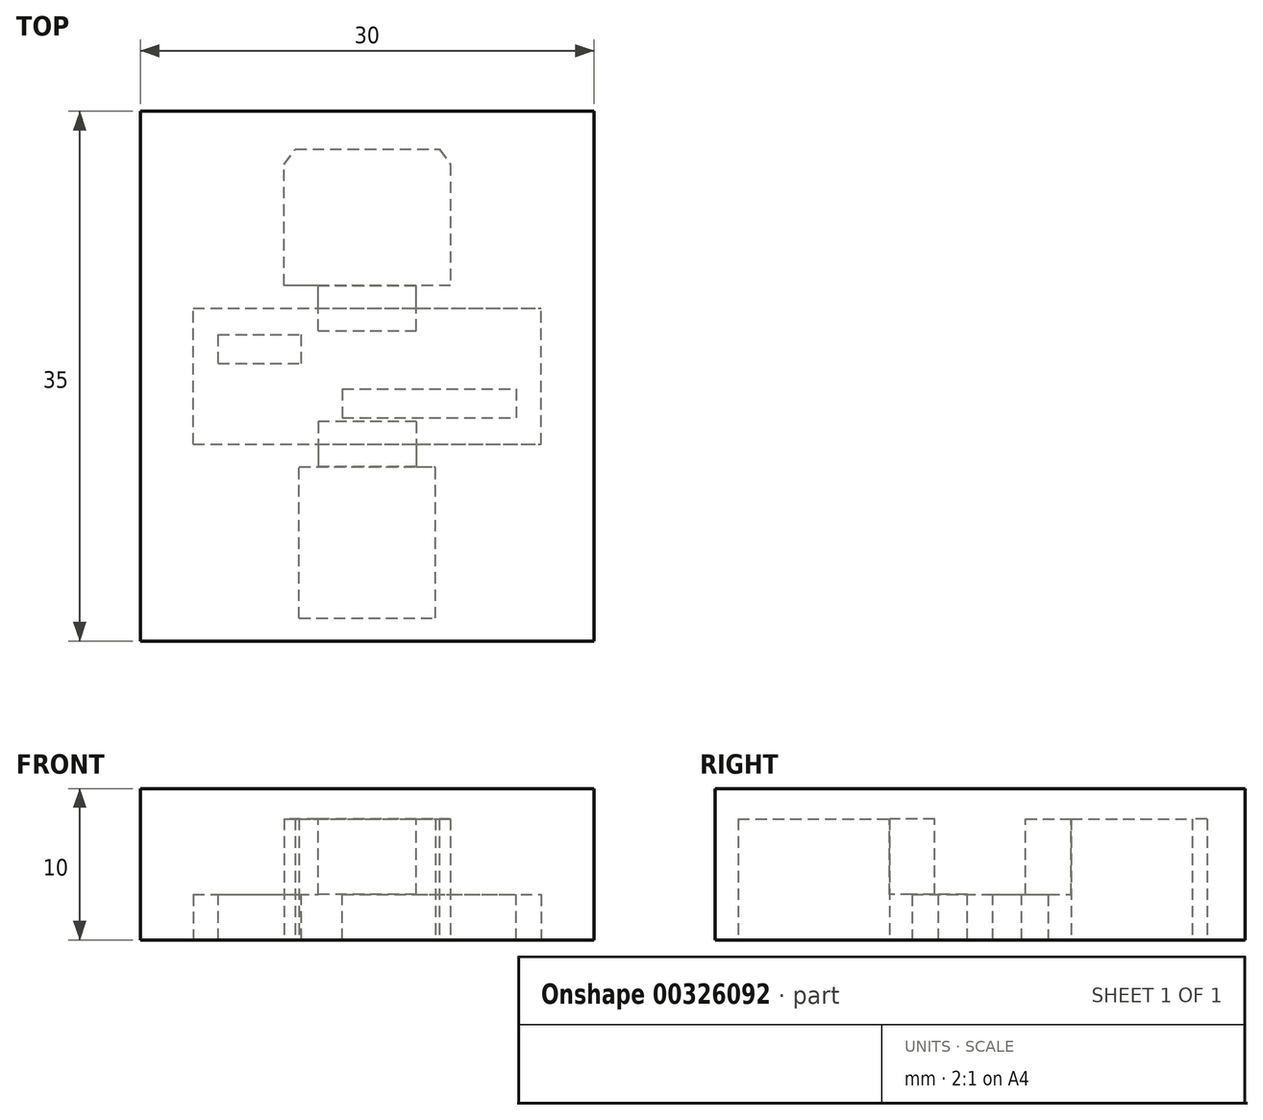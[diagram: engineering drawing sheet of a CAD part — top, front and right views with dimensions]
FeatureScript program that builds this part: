
annotation { "Feature Type Name" : "Feature", "Feature Type Description" : "" }
export const myFeature = defineFeature(function(context is Context, id is Id, definition is map)
    precondition{}
    {
        {
            var Q0;
            Q0=qCreatedBy(makeId("Top.planeOp"),FACE);
            var sketch = newSketch(context, id + "F0", { "sketchPlane" : qUnion([Q0])});
            skLineSegment(sketch, "E0.bottom", {"start": v(-15, 17.5) * mm, "end": v(15, 17.5) * mm});
            skLineSegment(sketch, "E0.top", {"start": v(-15, -17.5) * mm, "end": v(15, -17.5) * mm});
            skLineSegment(sketch, "E0.left", {"start": v(-15, 17.5) * mm, "end": v(-15, -17.5) * mm});
            skLineSegment(sketch, "E0.right", {"start": v(15, 17.5) * mm, "end": v(15, -17.5) * mm});
            skPoint(sketch, "E1", {"position": v(15, 0) * mm});
            skPoint(sketch, "E2", {"position": v(-15, 0) * mm});
            skPoint(sketch, "E3", {"position": v(0, 17.5) * mm});
            skSolve(sketch);
        }
        {
            var Q0;
            Q0=makeQuery(id+"F0.imprint","IMPRINT",FACE,{"disambiguationData":[TD([[makeQuery(id+"F0.imprint","IMPRINT",EDGE,{"derivedFrom":sQuery(id+"F0.wireOp",EDGE,"E0.bottom")}),-1.0]])]});
            var sketch = newSketch(context, id + "F1", { "sketchPlane" : qUnion([Q0])});
            skSolve(sketch);
        }
        {
            var Q0;
            Q0 = qSketchRegion(id + "F1", true);
            var Q1;
            Q1 = qSketchRegion(id + "F1", true);
            var Q2;
            Q2=makeQuery(id+"F1.imprint","IMPRINT",FACE,{"disambiguationData":[TD([[makeQuery(id+"F1.imprint","IMPRINT",EDGE,{"derivedFrom":makeQuery(id+"F0.imprint","IMPRINT",EDGE,{"derivedFrom":sQuery(id+"F0.wireOp",EDGE,"E0.bottom")})}),-1.0]])]});
            extrude(context, id + "F2", {"entities" : qUnion([Q0, Q1, Q2]), "depth" : 10 * mm});
        }
        {
            var Q0;
            Q0=makeQuery(id+"F0.imprint","IMPRINT",FACE,{"disambiguationData":[TD([[makeQuery(id+"F0.imprint","IMPRINT",EDGE,{"derivedFrom":sQuery(id+"F0.wireOp",EDGE,"E0.bottom")}),-1.0]])]});
            var sketch = newSketch(context, id + "F3", { "sketchPlane" : qUnion([Q0])});
            skLineSegment(sketch, "E4.bottom", {"start": v(-11.5, -4.5) * mm, "end": v(11.5, -4.5) * mm});
            skLineSegment(sketch, "E4.top", {"start": v(-11.5, 4.5) * mm, "end": v(11.5, 4.5) * mm});
            skLineSegment(sketch, "E4.left", {"start": v(-11.5, -4.5) * mm, "end": v(-11.5, 4.5) * mm});
            skLineSegment(sketch, "E4.right", {"start": v(11.5, -4.5) * mm, "end": v(11.5, 4.5) * mm});
            skPoint(sketch, "E5", {"position": v(11.5, 0) * mm});
            skPoint(sketch, "E6", {"position": v(0, -4.5) * mm});
            skSolve(sketch);
        }
        {
            var Q0;
            Q0=makeQuery(id+"F3.imprint","IMPRINT",FACE,{"disambiguationData":[TD([[makeQuery(id+"F3.imprint","IMPRINT",EDGE,{"derivedFrom":sQuery(id+"F3.wireOp",EDGE,"E4.bottom")}),1.0]])]});
            extrude(context, id + "F4", {"entities" : qUnion([Q0]), "operationType" : NewBodyOperationType.REMOVE, "depth" : 3 * mm});
        }
        {
            var Q0;
            Q0=makeQuery(id+"F0.imprint","IMPRINT",FACE,{"disambiguationData":[TD([[makeQuery(id+"F0.imprint","IMPRINT",EDGE,{"derivedFrom":sQuery(id+"F0.wireOp",EDGE,"E0.bottom")}),-1.0]])]});
            var sketch = newSketch(context, id + "F5", { "sketchPlane" : qUnion([Q0])});
            skLineSegment(sketch, "E7", {"start": v(-5.5, 6) * mm, "end": v(-5.5, 14) * mm});
            skLineSegment(sketch, "E8", {"start": v(-5.5, 14) * mm, "end": v(-4.75, 15) * mm});
            skLineSegment(sketch, "E9", {"start": v(-4.75, 15) * mm, "end": v(4.75, 15) * mm});
            skLineSegment(sketch, "E10", {"start": v(4.75, 15) * mm, "end": v(5.5, 14) * mm});
            skLineSegment(sketch, "E11", {"start": v(5.5, 14) * mm, "end": v(5.5, 6) * mm});
            skLineSegment(sketch, "E12", {"start": v(5.5, 6) * mm, "end": v(-5.5, 6) * mm});
            skPoint(sketch, "E13", {"position": v(0, 6) * mm});
            skPoint(sketch, "E14", {"position": v(0, 0) * mm});
            skSolve(sketch);
        }
        {
            var Q0;
            Q0=makeQuery(id+"F5.imprint","IMPRINT",FACE,{"disambiguationData":[TD([[makeQuery(id+"F5.imprint","IMPRINT",EDGE,{"derivedFrom":sQuery(id+"F5.wireOp",EDGE,"E7")}),-1.0]])]});
            extrude(context, id + "F6", {"entities" : qUnion([Q0]), "operationType" : NewBodyOperationType.REMOVE, "depth" : 8 * mm});
        }
        {
            var Q0;
            Q0=makeQuery(id+"F0.imprint","IMPRINT",FACE,{"disambiguationData":[TD([[makeQuery(id+"F0.imprint","IMPRINT",EDGE,{"derivedFrom":sQuery(id+"F0.wireOp",EDGE,"E0.bottom")}),-1.0]])]});
            var sketch = newSketch(context, id + "F7", { "sketchPlane" : qUnion([Q0])});
            skLineSegment(sketch, "E15.bottom", {"start": v(-4.5, -16) * mm, "end": v(4.5, -16) * mm});
            skLineSegment(sketch, "E15.top", {"start": v(-4.5, -6) * mm, "end": v(4.5, -6) * mm});
            skLineSegment(sketch, "E15.left", {"start": v(-4.5, -16) * mm, "end": v(-4.5, -6) * mm});
            skLineSegment(sketch, "E15.right", {"start": v(4.5, -16) * mm, "end": v(4.5, -6) * mm});
            skPoint(sketch, "E16", {"position": v(0, -16) * mm});
            skSolve(sketch);
        }
        {
            var Q0;
            Q0=makeQuery(id+"F7.imprint","IMPRINT",FACE,{"disambiguationData":[TD([[makeQuery(id+"F7.imprint","IMPRINT",EDGE,{"derivedFrom":sQuery(id+"F7.wireOp",EDGE,"E15.bottom")}),1.0]])]});
            extrude(context, id + "F8", {"entities" : qUnion([Q0]), "operationType" : NewBodyOperationType.REMOVE, "depth" : 8 * mm});
        }
        {
            var Q0;
            Q0=makeQuery(id+"F4.boolean.opBoolean","COPY",FACE,{"derivedFrom":makeQuery(id+"F4.opExtrude","CAP_FACE",FACE,{"disambiguationData":[OSD([sQuery(id+"F3.wireOp",EDGE,"E4.bottom"),sQuery(id+"F3.wireOp",EDGE,"E4.top"),sQuery(id+"F3.wireOp",EDGE,"E4.left"),sQuery(id+"F3.wireOp",EDGE,"E4.right")])],"isStart":false})});
            var sketch = newSketch(context, id + "F9", { "sketchPlane" : qUnion([Q0])});
            skLineSegment(sketch, "E17.bottom", {"start": v(-9.85, -0.85) * mm, "end": v(-4.35, -0.85) * mm});
            skLineSegment(sketch, "E17.top", {"start": v(-9.85, -2.75) * mm, "end": v(-4.35, -2.75) * mm});
            skLineSegment(sketch, "E17.left", {"start": v(-9.85, -0.85) * mm, "end": v(-9.85, -2.75) * mm});
            skLineSegment(sketch, "E17.right", {"start": v(-4.35, -0.85) * mm, "end": v(-4.35, -2.75) * mm});
            skLineSegment(sketch, "E18.bottom", {"start": v(-1.65, 0.85) * mm, "end": v(4.1, 0.85) * mm});
            skLineSegment(sketch, "E18.top", {"start": v(-1.65, 2.75) * mm, "end": v(4.1, 2.75) * mm});
            skLineSegment(sketch, "E18.left", {"start": v(-1.65, 0.85) * mm, "end": v(-1.65, 2.75) * mm});
            skLineSegment(sketch, "E18.right", {"start": v(4.1, 0.85) * mm, "end": v(4.1, 2.75) * mm});
            skLineSegment(sketch, "E19.bottom", {"start": v(-1.65, -0.85) * mm, "end": v(4.1, -0.85) * mm});
            skLineSegment(sketch, "E19.top", {"start": v(-1.65, -2.75) * mm, "end": v(4.1, -2.75) * mm});
            skLineSegment(sketch, "E19.left", {"start": v(-1.65, -0.85) * mm, "end": v(-1.65, -2.75) * mm});
            skLineSegment(sketch, "E19.right", {"start": v(4.1, -0.85) * mm, "end": v(4.1, -2.75) * mm});
            skLineSegment(sketch, "E20.bottom", {"start": v(4.1, 0.85) * mm, "end": v(9.85, 0.85) * mm});
            skLineSegment(sketch, "E20.top", {"start": v(4.1, 2.75) * mm, "end": v(9.85, 2.75) * mm});
            skLineSegment(sketch, "E20.right", {"start": v(9.85, 0.85) * mm, "end": v(9.85, 2.75) * mm});
            skLineSegment(sketch, "E21.bottom", {"start": v(4.1, -0.85) * mm, "end": v(9.85, -0.85) * mm});
            skLineSegment(sketch, "E21.top", {"start": v(4.1, -2.75) * mm, "end": v(9.85, -2.75) * mm});
            skLineSegment(sketch, "E21.right", {"start": v(9.85, -0.85) * mm, "end": v(9.85, -2.75) * mm});
            skLineSegment(sketch, "E22", {"start": v(-9.85, -2.75) * mm, "end": v(9.85, -2.75) * mm, "construction": true});
            skPoint(sketch, "E23", {"position": v(0, -2.75) * mm});
            skLineSegment(sketch, "E24", {"start": v(9.85, 2.75) * mm, "end": v(9.85, -2.75) * mm, "construction": true});
            skPoint(sketch, "E25", {"position": v(9.85, 0) * mm});
            skSolve(sketch);
        }
        {
            var Q0;
            Q0=makeQuery(id+"F9.imprint","IMPRINT",FACE,{"disambiguationData":[TD([[makeQuery(id+"F9.imprint","IMPRINT",EDGE,{"derivedFrom":sQuery(id+"F9.wireOp",EDGE,"E20.bottom")}),1.0]])]});
            var Q1;
            Q1=makeQuery(id+"F9.imprint","IMPRINT",FACE,{"disambiguationData":[TD([[makeQuery(id+"F9.imprint","IMPRINT",EDGE,{"derivedFrom":sQuery(id+"F9.wireOp",EDGE,"E17.bottom")}),-1.0]])]});
            var Q2;
            Q2=makeQuery(id+"F9.imprint","IMPRINT",FACE,{"disambiguationData":[TD([[makeQuery(id+"F9.imprint","IMPRINT",EDGE,{"derivedFrom":sQuery(id+"F9.wireOp",EDGE,"E18.bottom")}),1.0]])]});
            var Q3;
            Q3=makeQuery(id+"F2.opExtrude","CAP_FACE",FACE,{"disambiguationData":[OSD([sQuery(id+"F0.wireOp",EDGE,"E0.bottom"),sQuery(id+"F0.wireOp",EDGE,"E0.top"),sQuery(id+"F0.wireOp",EDGE,"E0.left"),sQuery(id+"F0.wireOp",EDGE,"E0.right")])],"isStart":true});
            extrude(context, id + "F10", {"entities" : qUnion([Q0, Q1, Q2]), "operationType" : NewBodyOperationType.ADD, "endBound" : BoundingType.UP_TO_SURFACE, "endBoundEntityFace" : qUnion([Q3]), "depth" : 25 * mm});
        }
        {
            var Q0;
            Q0=makeQuery(id+"F6.boolean.opBoolean","COPY",FACE,{"derivedFrom":makeQuery(id+"F6.opExtrude","SWEPT_FACE",FACE,{"disambiguationData":[OSD([sQuery(id+"F5.wireOp",EDGE,"E12")])]})});
            var sketch = newSketch(context, id + "F11", { "sketchPlane" : qUnion([Q0])});
            skLineSegment(sketch, "E26.bottom", {"start": v(3.25, 3) * mm, "end": v(-3.25, 3) * mm});
            skLineSegment(sketch, "E26.top", {"start": v(3.25, 8) * mm, "end": v(-3.25, 8) * mm});
            skLineSegment(sketch, "E26.left", {"start": v(3.25, 3) * mm, "end": v(3.25, 8) * mm});
            skLineSegment(sketch, "E26.right", {"start": v(-3.25, 3) * mm, "end": v(-3.25, 8) * mm});
            skPoint(sketch, "E27", {"position": v(0, 3) * mm});
            skPoint(sketch, "E28", {"position": v(0, 0) * mm});
            skSolve(sketch);
        }
        {
            var Q0;
            Q0=makeQuery(id+"F11.imprint","IMPRINT",FACE,{"disambiguationData":[TD([[makeQuery(id+"F11.imprint","IMPRINT",EDGE,{"derivedFrom":sQuery(id+"F11.wireOp",EDGE,"E26.bottom")}),-1.0]])]});
            extrude(context, id + "F12", {"entities" : qUnion([Q0]), "operationType" : NewBodyOperationType.REMOVE, "oppositeDirection" : true, "depth" : 3 * mm});
        }
        {
            var Q0;
            Q0=makeQuery(id+"F8.boolean.opBoolean","COPY",FACE,{"derivedFrom":makeQuery(id+"F8.opExtrude","SWEPT_FACE",FACE,{"disambiguationData":[OSD([sQuery(id+"F7.wireOp",EDGE,"E15.top")])]})});
            var sketch = newSketch(context, id + "F13", { "sketchPlane" : qUnion([Q0])});
            skLineSegment(sketch, "E29.bottom", {"start": v(3.25, 3) * mm, "end": v(-3.25, 3) * mm});
            skLineSegment(sketch, "E29.top", {"start": v(3.25, 8) * mm, "end": v(-3.25, 8) * mm});
            skLineSegment(sketch, "E29.left", {"start": v(3.25, 3) * mm, "end": v(3.25, 8) * mm});
            skLineSegment(sketch, "E29.right", {"start": v(-3.25, 3) * mm, "end": v(-3.25, 8) * mm});
            skPoint(sketch, "E30", {"position": v(0, 3) * mm});
            skPoint(sketch, "E31", {"position": v(0, 0) * mm});
            skSolve(sketch);
        }
        {
            var Q0;
            Q0=makeQuery(id+"F13.imprint","IMPRINT",FACE,{"disambiguationData":[TD([[makeQuery(id+"F13.imprint","IMPRINT",EDGE,{"derivedFrom":sQuery(id+"F13.wireOp",EDGE,"E29.bottom")}),-1.0]])]});
            extrude(context, id + "F14", {"entities" : qUnion([Q0]), "operationType" : NewBodyOperationType.REMOVE, "oppositeDirection" : true, "depth" : 3 * mm});
        }
    });
